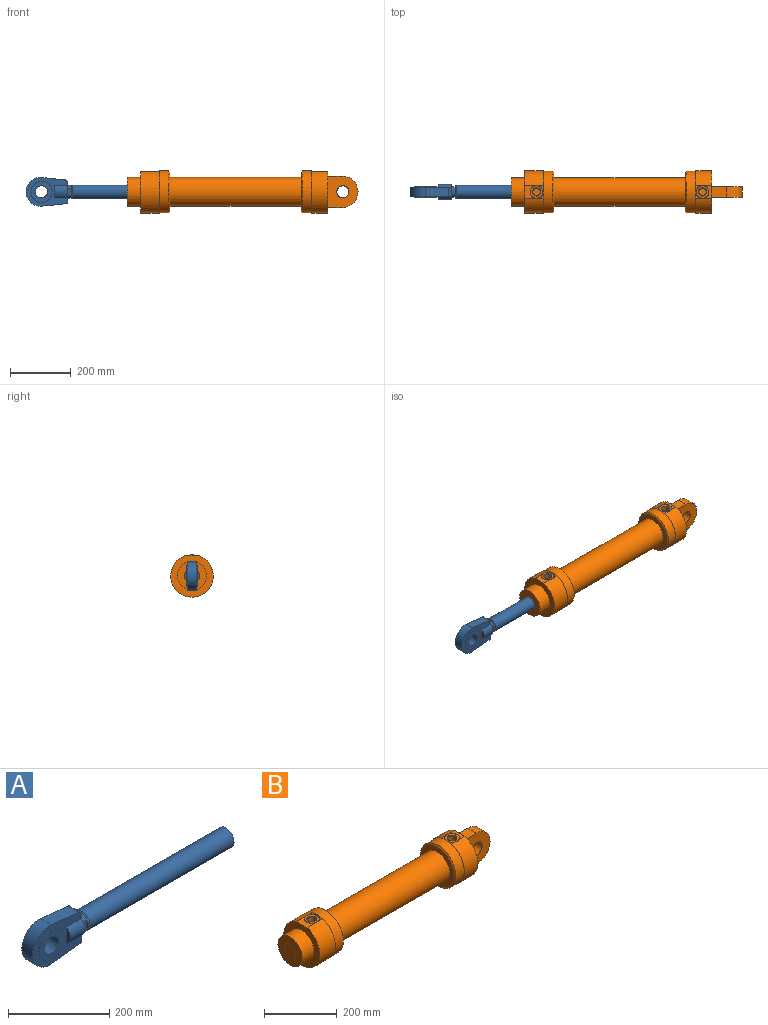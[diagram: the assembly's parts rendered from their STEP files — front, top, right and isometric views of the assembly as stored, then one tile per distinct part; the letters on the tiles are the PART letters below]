
ASSEMBLY  parts=2 mates=1
PART A: 45 faces, bbox 556x50x95 mm
  f0: cylinder r=20mm len=40mm, axis (0,-1,0), area 4398.2mm2, adj f1,f2
  f1: plane 70x70mm, normal (0,1,0), area 2591.8mm2, adj f0,f3
  f2: plane 70x70mm, normal (0,-1,0), area 2591.8mm2, adj f0,f5
  f3: cylinder r=35mm len=70mm, axis (0,-1,0), area 549.8mm2, adj f1,f12
  f4: plane 40x10mm, normal (-1,0,0), area 279.6mm2, adj f11,f12
  f5: cylinder r=35mm len=70mm, axis (0,-1,0), area 549.8mm2, adj f2,f15
  f6: plane 40x10mm, normal (-1,0,0), area 279.6mm2, adj f14,f15
  f7: plane 79.97x30mm, normal (0.1,0,-0.99), area 2412.3mm2, adj f8,f12,f13,f15
  f8: cylinder r=47.5mm len=95mm, axis (0,-1,0), area 4773.9mm2, adj f7,f9,f12,f15
  f9: plane 75.49x30mm, normal (0.1,0,0.99), area 2277.2mm2, adj f8,f10,f12,f15
  f10: cylinder r=9mm len=30mm, axis (0,-1,0), area 396mm2, adj f9,f12,f15,f16
  f11: cylinder r=25mm len=41mm, axis (1,0,0), area 1901mm2, adj f4,f12,f16
  f12: plane 136x95mm, normal (0,1,0), area 5672.5mm2, adj f3,f4,f7,f8,f9,f10,f11,f13
  f13: cylinder r=4mm len=30mm, axis (0,-1,0), area 176mm2, adj f7,f12,f15,f16
  f14: cylinder r=25mm len=41mm, axis (1,0,0), area 1901mm2, adj f6,f15,f16
  f15: plane 136x95mm, normal (0,-1,0), area 5672.5mm2, adj f5,f6,f7,f8,f9,f10,f13,f14
  f16: plane 65.29x50mm, normal (1,0,0), area 1178.1mm2, adj f10,f11,f12,f13,f14,f15,f17,f18
  f17: cone r=21.49mm half-angle=45deg, axis (1,0,0), area 0.6mm2, adj f16,f18,f19,f22
  f18: plane 23.52x13mm, normal (0,-1,0), area 305.7mm2, adj f16,f17,f20,f21,f22,f24
  f19: plane 23.52x13mm, normal (0,1,0), area 305.7mm2, adj f16,f17,f20,f22,f23,f24
  f20: cone r=21.49mm half-angle=45deg, axis (1,0,0), area 0.6mm2, adj f16,f18,f19,f24
  f21: plane 23.52x3.5mm, normal (-1,0,0), area 55.8mm2, adj f18,f25
  f22: cylinder r=21.5mm len=36mm, axis (1,0,0), area 554.2mm2, adj f17,f18,f19,f25
  f23: plane 23.52x3.5mm, normal (-1,0,0), area 55.8mm2, adj f19,f25
  f24: cylinder r=21.5mm len=36mm, axis (1,0,0), area 554.2mm2, adj f18,f19,f20,f25
  f25: cone r=22mm half-angle=15deg, axis (1,0,0), area 534.1mm2, adj f21,f22,f23,f24,f26
  f26: cylinder r=22.5mm len=403.27mm, axis (1,0,0), area 57010.7mm2, adj f25,f27
  f27: plane 45x45mm, normal (1,0,0), area 1590.4mm2, adj f26
  f28: plane 65x65mm, normal (0,1,0), area 299.2mm2, adj f30,f31
  f29: plane 65x65mm, normal (0,-1,0), area 299.2mm2, adj f30,f31
  f30: cylinder r=32.5mm len=65mm, axis (0,-1,0), area 439mm2, adj f28,f29
  f31: cylinder r=31mm len=62mm, axis (0,-1,0), area 418.8mm2, adj f28,f29
  f32: cylinder r=32.5mm len=65mm, axis (0,-1,0), area 439mm2, adj f33,f34
  f33: plane 65x65mm, normal (0,-1,0), area 299.2mm2, adj f32,f35
  f34: plane 65x65mm, normal (0,1,0), area 299.2mm2, adj f32,f35
  f35: cylinder r=31mm len=62mm, axis (0,-1,0), area 418.8mm2, adj f33,f34
  f36: plane 33.16x33.16mm, normal (1,0,0), area 23.8mm2, adj f38,f40
  f37: plane 33.38x33.38mm, normal (-1,0,0), area 35.1mm2, adj f39,f40
  f38: cone r=16.58mm half-angle=45deg, axis (-1,0,0), area 16mm2, adj f36,f39
  f39: cylinder r=16.69mm len=33.38mm, axis (-1,0,0), area 346.9mm2, adj f37,f38
  f40: cylinder r=16.35mm len=32.7mm, axis (1,0,0), area 328.7mm2, adj f36,f37
  f41: plane 33.16x33.16mm, normal (-1,0,0), area 863.6mm2, adj f42
  f42: cone r=16.58mm half-angle=45deg, axis (1,0,0), area 16mm2, adj f41,f44
  f43: plane 33.38x33.38mm, normal (1,0,0), area 874.9mm2, adj f44
  f44: cylinder r=16.69mm len=33.38mm, axis (-1,0,0), area 116.2mm2, adj f42,f43
PART B: 46 faces, bbox 760x140x139 mm
  f0: cylinder r=70mm len=140mm, axis (1,0,0), area 20723.4mm2, adj f1,f14,f21,f29,f34
  f1: cylinder r=21mm len=42mm, axis (0,0,-1), area 62.7mm2, adj f0,f21,f29,f36
  f2: cylinder r=12.12mm len=24.25mm, axis (0,0,-1), area 1502.7mm2, adj f5,f26
  f3: plane 104x100mm, normal (0,1,0), area 7982.8mm2, adj f14,f17,f18,f28,f32
  f4: cone r=13.4mm half-angle=45deg, axis (0,0,1), area 144.6mm2, adj f22,f36
  f5: plane 24.25x24.25mm, normal (0,0,1), area 461.9mm2, adj f2
  f6: cylinder r=47.5mm len=432mm, axis (1,0,0), area 128931mm2, adj f11,f15
  f7: cylinder r=21mm len=42mm, axis (0,0,-1), area 63.1mm2, adj f25,f27,f30,f31
  f8: plane 140x137mm, normal (-1,0,0), area 8224.1mm2, adj f27,f31,f35
  f9: cylinder r=69mm len=138mm, axis (-1,0,0), area 13922.4mm2, adj f10,f24,f34
  f10: cone r=64mm half-angle=60deg, axis (1,0,0), area 2412.4mm2, adj f9,f11
  f11: plane 128x128mm, normal (-1,0,0), area 5779.7mm2, adj f6,f10
  f12: plane 95x95mm, normal (-1,0,0), area 5497.8mm2, adj f35,f37
  f13: plane 32.99x2mm, normal (-1,0,0), area 44.1mm2, adj f23,f30
  f14: plane 140x137mm, normal (1,0,0), area 11672.4mm2, adj f0,f3,f18,f19,f21,f28
  f15: plane 128x128mm, normal (1,0,0), area 5779.7mm2, adj f6,f33
  f16: plane 140x137mm, normal (1,0,0), area 399.3mm2, adj f23,f30,f31
  f17: cylinder r=20mm len=40mm, axis (0,-1,0), area 4398.2mm2, adj f3,f19
  f18: plane 48x35mm, normal (0,0,1), area 1680mm2, adj f3,f14,f19,f32
  f19: plane 104x100mm, normal (0,-1,0), area 7982.8mm2, adj f14,f17,f18,f28,f32
  f20: plane 24.25x24.25mm, normal (0,0,1), area 461.9mm2, adj f22
  f21: plane 40.55x24.52mm, normal (0,0,1), area 529mm2, adj f0,f1,f14
  f22: cylinder r=12.12mm len=24.25mm, axis (0,0,-1), area 1502.7mm2, adj f4,f20
  f23: cylinder r=69mm len=138mm, axis (1,0,0), area 13922.4mm2, adj f13,f16,f33
  f24: plane 32.99x2mm, normal (1,0,0), area 44.1mm2, adj f9,f29
  f25: plane 42x42mm, normal (0,0,1), area 821.3mm2, adj f7,f26
  f26: cone r=13.4mm half-angle=45deg, axis (0,0,1), area 144.6mm2, adj f2,f25
  f27: plane 40.55x33.52mm, normal (0,0,1), area 893.9mm2, adj f7,f8,f31
  f28: plane 48x35mm, normal (0,0,-1), area 1680mm2, adj f3,f14,f19,f32
  f29: plane 40.55x16.52mm, normal (0,0,1), area 204.6mm2, adj f0,f1,f24,f34
  f30: plane 40.55x16.52mm, normal (0,0,1), area 204.6mm2, adj f7,f13,f16,f31
  f31: cylinder r=70mm len=140mm, axis (1,0,0), area 24310.2mm2, adj f7,f8,f16,f27,f30
  f32: cylinder r=52mm len=104mm, axis (0,1,0), area 5717.7mm2, adj f3,f18,f19,f28
  f33: cone r=64mm half-angle=60deg, axis (-1,0,0), area 2412.4mm2, adj f15,f23
  f34: plane 140x137mm, normal (-1,0,0), area 399.3mm2, adj f0,f9,f29
  f35: cylinder r=47.5mm len=95mm, axis (1,0,0), area 13430.3mm2, adj f8,f12
  f36: plane 42x42mm, normal (0,0,1), area 821.3mm2, adj f1,f4
  f37: plane 45x45mm, normal (-1,0,0), area 1590.4mm2, adj f12
  f38: plane 63.5x63.5mm, normal (0,1,0), area 147.9mm2, adj f39,f41
  f39: cylinder r=31.75mm len=63.5mm, axis (0,-1,0), area 319.2mm2, adj f38,f40
  f40: plane 63.5x63.5mm, normal (0,-1,0), area 147.9mm2, adj f39,f41
  f41: cylinder r=31mm len=62mm, axis (0,-1,0), area 311.6mm2, adj f38,f40
  f42: plane 63.5x63.5mm, normal (0,-1,0), area 147.9mm2, adj f44,f45
  f43: plane 63.5x63.5mm, normal (0,1,0), area 147.9mm2, adj f44,f45
  f44: cylinder r=31mm len=62mm, axis (0,-1,0), area 311.6mm2, adj f42,f43
  f45: cylinder r=31.75mm len=63.5mm, axis (0,-1,0), area 319.2mm2, adj f42,f43
PLACE A t=(-176.41,0,0)mm
PLACE B at identity fixed
MATE slider A.f11 <-> B.f0  axis (1,0,0) through (117.59,0,0)mm
